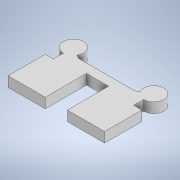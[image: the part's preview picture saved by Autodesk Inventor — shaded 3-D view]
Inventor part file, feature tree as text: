
AUTODESK INVENTOR PART (.ipt)
format: ipt  version: 2020 (Build 240168000, 168)  size: 136,192 bytes
history: native  units: mm
features: other x2, extrude x1, sketch x1
ambient origin geometry x8: Origin, YZ Plane, XZ Plane, XY Plane, X Axis, Y Axis, Z Axis, Center Point
bodies: Body1 (feature_tree)
feature tree (4):
  other  "Bryła1"
  extrude  "Wyciągnięcie proste1"  Depth=9.0mm
  other  "Pogrubienie2"
  sketch  "Szkic1"
